# Revit family: Patio-Door_3-Light_OXO-Element-2-0_Novatech
name_source: partatom
category: Doors
units: mm (PartAtom-declared; Revit-internal decimal feet)

## family parameters
Always vertical = Yes
Classification Number = 23.30.10.00
Cut with Voids When Loaded = No
Host = Wall
Room Calculation Point = No
Shared = No

## types (20) — shared parameters
Analytic Construction = <None>
CAD Details = https://www.arcat.com
Define Thermal Properties by = Schematic Type
Function = Interior
Glass = Glass
Keynote = 08 32 00
Manufacturer = Novatech
Model = Element 2.0
Product Page URL = https://www.arcat.com
Specification = https://www.arcat.com
URL = https://www.groupenovatech.com
Wall Closure = By host

## per-type parameters (varying)
| type | Door Height | Door Width | Frame Material | Height | Height Sash | Width | Width Sash |
| Black - 141 5/8" x 81" | 77.42" | 47.21" | Black | 81.00" | 77.42" | 141.63" | 47.21" |
| Black - 107 3/16" x 95 1/2" | 91.92" | 35.73" | Black | 95.50" | 91.92" | 107.19" | 35.73" |
| Black - 107 3/16" x 79 1/2" | 75.92" | 35.73" | Black | 79.50" | 75.92" | 107.19" | 35.73" |
| Black - 105 5/8" x 81" | 77.42" | 35.21" | Black | 81.00" | 77.42" | 105.63" | 35.21" |
| Commercial Brown - 141 5/8" x 81" | 77.42" | 47.21" | Commercial Brown | 81.00" | 77.42" | 141.63" | 47.21" |
| Commercial Brown - 107 3/16" x 95 1/2" | 91.92" | 35.73" | Commercial Brown | 95.50" | 91.92" | 107.19" | 35.73" |
| Commercial Brown - 107 3/16" x 79 1/2" | 75.92" | 35.73" | Commercial Brown | 79.50" | 75.92" | 107.19" | 35.73" |
| Commercial Brown - 105 5/8" x 81" | 77.42" | 35.21" | Commercial Brown | 81.00" | 77.42" | 105.63" | 35.21" |
| Charcoal - 141 5/8" x 81" | 77.42" | 47.21" | Charcoal | 81.00" | 77.42" | 141.63" | 47.21" |
| Charcoal - 107 3/16" x 95 1/2" | 91.92" | 35.73" | Charcoal | 95.50" | 91.92" | 107.19" | 35.73" |
| Charcoal - 107 3/16" x 79 1/2" | 75.92" | 35.73" | Charcoal | 79.50" | 75.92" | 107.19" | 35.73" |
| Charcoal - 105 5/8" x 81" | 77.42" | 35.21" | Charcoal | 81.00" | 77.42" | 105.63" | 35.21" |
| Clear anodized - 141 5/8" x 81" | 77.42" | 47.21" | Clear anodized | 81.00" | 77.42" | 141.63" | 47.21" |
| Clear anodized - 107 3/16" x 95 1/2" | 91.92" | 35.73" | Clear anodized | 95.50" | 91.92" | 107.19" | 35.73" |
| Clear anodized - 107 3/16" x 79 1/2" | 75.92" | 35.73" | Clear anodized | 79.50" | 75.92" | 107.19" | 35.73" |
| Clear anodized - 105 5/8" x 81" | 77.42" | 35.21" | Clear anodized | 81.00" | 77.42" | 105.63" | 35.21" |
| White (Blue tint) - 141 5/8" x 81" | 77.42" | 47.21" | White (Blue tint) | 81.00" | 77.42" | 141.63" | 47.21" |
| White (Blue tint) - 107 3/16" x 95 1/2" | 91.92" | 35.73" | White (Blue tint) | 95.50" | 91.92" | 107.19" | 35.73" |
| White (Blue tint) - 105 5/8" x 81" | 77.42" | 35.21" | White (Blue tint) | 81.00" | 77.42" | 105.63" | 35.21" |
| White (Blue tint) - 107 3/16" x 79 1/2" | 75.92" | 35.73" | White (Blue tint) | 79.50" | 75.92" | 107.19" | 35.73" |

## geometry (parser evidence)
native form markers: Sweep x18
no freeform markers — native parametric forms only
